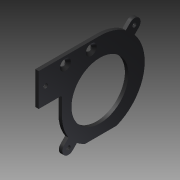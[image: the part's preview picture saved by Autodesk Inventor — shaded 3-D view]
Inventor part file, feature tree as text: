
AUTODESK INVENTOR PART (.ipt)
format: ipt  version: 2015 (Build 190159000, 159)  size: 166,912 bytes
history: native  units: mm
features: extrude x3, hole x3, reference x1
ambient origin geometry x8: Origin, YZ Plane, XZ Plane, XY Plane, X Axis, Y Axis, Z Axis, Center Point
bodies: Solid1 (feature_tree)
feature tree (7):
  extrude  "Extrusión1"  Depth=2.0mm
  extrude  "Extrusión2"  Depth=65.0mm TaperAngle=0.0deg
  hole  "Agujero1"  [1 undecoded]
  hole  "Agujero3"  [1 undecoded]
  hole  "Agujero5"  [1 undecoded]
  extrude  "Extrusión3"  Depth=12.5mm
  reference  "Referencia2"
note: 3 required parameter values undecoded (feature->parameter linkage not recoverable at this tier; creation-order binding heuristic only, values carry confidence <= 0.55)
